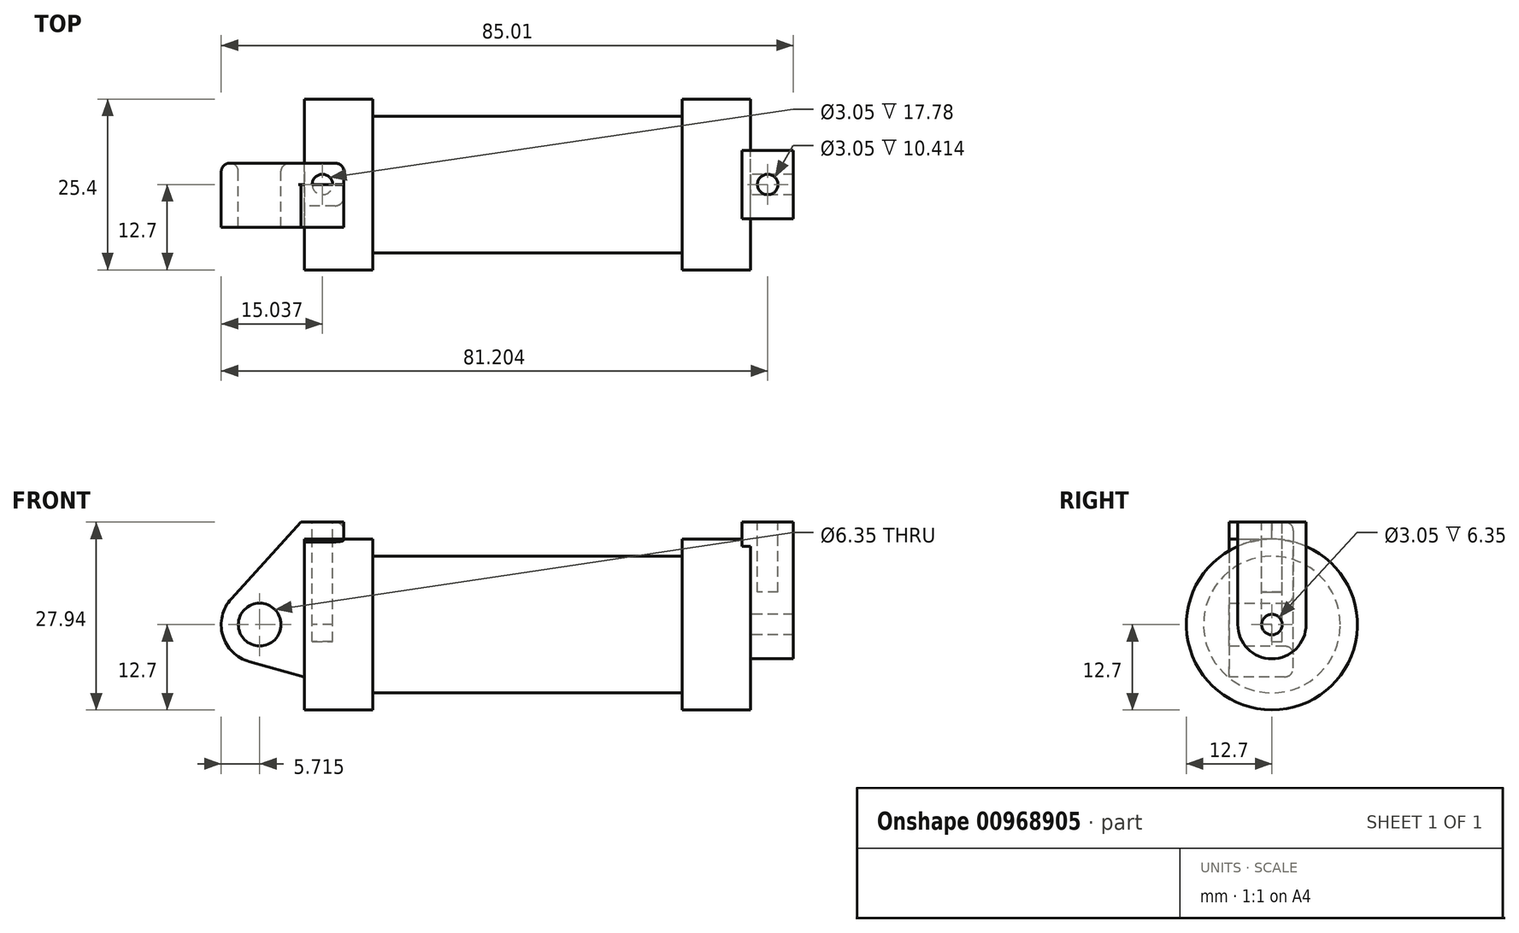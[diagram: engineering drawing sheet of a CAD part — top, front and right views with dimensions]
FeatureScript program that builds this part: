
annotation { "Feature Type Name" : "Feature", "Feature Type Description" : "" }
export const myFeature = defineFeature(function(context is Context, id is Id, definition is map)
    precondition{}
    {
        {
            var Q0;
            Q0=qCreatedBy(makeId("Front.planeOp"),FACE);
            var sketch = newSketch(context, id + "F0", { "sketchPlane" : qUnion([Q0])});
            skLineSegment(sketch, "E0", {"start": v(0, 0) * mm, "end": v(0, 12.7) * mm});
            skLineSegment(sketch, "E1", {"start": v(0, 12.7) * mm, "end": v(10.16, 12.7) * mm});
            skLineSegment(sketch, "E2", {"start": v(10.16, 12.7) * mm, "end": v(10.16, 10.16) * mm});
            skLineSegment(sketch, "E3", {"start": v(10.16, 10.16) * mm, "end": v(56.13, 10.16) * mm});
            skLineSegment(sketch, "E4", {"start": v(56.13, 10.16) * mm, "end": v(56.13, 12.7) * mm});
            skLineSegment(sketch, "E5", {"start": v(56.13, 12.7) * mm, "end": v(66.3, 12.7) * mm});
            skLineSegment(sketch, "E6", {"start": v(66.3, 12.7) * mm, "end": v(66.3, 0) * mm});
            skLineSegment(sketch, "E7", {"start": v(66.3, 0) * mm, "end": v(0, 0) * mm});
            skLineSegment(sketch, "E8", {"start": v(5.84, 15.24) * mm, "end": v(-0.5, 15.24) * mm});
            skLineSegment(sketch, "E9", {"start": v(-0.5, 15.24) * mm, "end": v(-10.88, 3.85) * mm});
            skLineSegment(sketch, "E10", {"start": v(0, 0) * mm, "end": v(-6.65, 0) * mm});
            skCircle(sketch, "E11", {"center": v(-6.65, 0) * mm, "radius": 5.72 * mm});
            skCircle(sketch, "E12", {"center": v(-6.65, 0) * mm, "radius": 3.18 * mm});
            skLineSegment(sketch, "E13", {"start": v(5.84, 15.24) * mm, "end": v(5.84, -9.4) * mm});
            skLineSegment(sketch, "E14", {"start": v(5.84, -9.4) * mm, "end": v(-8.18, -5.5) * mm});
            skSolve(sketch);
        }
        {
            var Q0;
            {var subQ1=sQuery(id+"F0.wireOp",EDGE,"E0");Q0=makeQuery(id+"F0.imprint","IMPRINT",FACE,{"disambiguationData":[TD([[makeQuery(id+"F0.imprint","IMPRINT",EDGE,{"derivedFrom":subQ1}),1.0]])]});}
            var Q1;
            {var subQ0=sQuery(id+"F0.wireOp",EDGE,"E0");Q1=makeQuery(id+"F0.imprint","IMPRINT",FACE,{"disambiguationData":[TD([[makeQuery(id+"F0.imprint","IMPRINT",EDGE,{"derivedFrom":subQ0}),-1.0]])]});}
            var Q2;
            {var subQ0=sQuery(id+"F0.wireOp",EDGE,"E14");Q2=makeQuery(id+"F0.imprint","IMPRINT",FACE,{"disambiguationData":[TD([[makeQuery(id+"F0.imprint","IMPRINT",EDGE,{"derivedFrom":subQ0}),-1.0]])]});}
            var Q3;
            {var subQ5=sQuery(id+"F0.wireOp",EDGE,"E12");Q3=makeQuery(id+"F0.imprint","IMPRINT",FACE,{"disambiguationData":[TD([[makeQuery(id+"F0.imprint","IMPRINT",EDGE,{"derivedFrom":subQ5}),-1.0]])]});}
            extrude(context, id + "F1", {"entities" : qUnion([Q0, Q1, Q2, Q3]), "endBound" : BoundingType.SYMMETRIC, "depth" : 6.35 * mm, "offsetDistance" : 25.4 * mm});
        }
        {
            var Q0;
            {var subQ0=sQuery(id+"F0.wireOp",EDGE,"E2");Q0=makeQuery(id+"F0.imprint","IMPRINT",FACE,{"disambiguationData":[TD([[makeQuery(id+"F0.imprint","IMPRINT",EDGE,{"derivedFrom":subQ0}),-1.0]])]});}
            var Q1;
            {var subQ0=sQuery(id+"F0.wireOp",EDGE,"E0");Q1=makeQuery(id+"F0.imprint","IMPRINT",FACE,{"disambiguationData":[TD([[makeQuery(id+"F0.imprint","IMPRINT",EDGE,{"derivedFrom":subQ0}),-1.0]])]});}
            var Q2;
            Q2=sQuery(id+"F0.wireOp",EDGE,"E7");
            revolve(context, id + "F2", {"surfaceOperationType" : NewSurfaceOperationType.NEW, "entities" : qUnion([Q0, Q1]), "axis" : qUnion([Q2]), "revolveType" : RevolveType.FULL});
        }
        {
            var Q0;
            Q0=makeQuery(id+"F2.opRevolve","SWEPT_FACE",FACE,{"disambiguationData":[OSD([sQuery(id+"F0.wireOp",EDGE,"E6")])]});
            var sketch = newSketch(context, id + "F3", { "sketchPlane" : qUnion([Q0])});
            skCircle(sketch, "E15", {"center": v(0, 0) * mm, "radius": 1.52 * mm});
            skCircle(sketch, "E16", {"center": v(0, 0) * mm, "radius": 5.08 * mm});
            skLineSegment(sketch, "E17", {"start": v(5.08, 0) * mm, "end": v(5.08, 15.24) * mm});
            skLineSegment(sketch, "E18", {"start": v(-5.08, 0) * mm, "end": v(-5.08, 15.24) * mm});
            skLineSegment(sketch, "E19", {"start": v(-5.08, 15.24) * mm, "end": v(5.08, 15.24) * mm});
            skSolve(sketch);
        }
        {
            var Q0;
            {var subQ0=sQuery(id+"F3.wireOp",EDGE,"E19");Q0=makeQuery(id+"F3.imprint","IMPRINT",FACE,{"disambiguationData":[TD([[makeQuery(id+"F3.imprint","IMPRINT",EDGE,{"derivedFrom":subQ0}),-1.0]])]});}
            extrude(context, id + "F4", {"entities" : qUnion([Q0]), "operationType" : NewBodyOperationType.ADD, "depth" : -1.27 * mm, "offsetDistance" : 25.4 * mm});
        }
        {
            var Q0;
            Q0 = qSketchRegion(id + "F3", true);
            extrude(context, id + "F5", {"entities" : qUnion([Q0]), "operationType" : NewBodyOperationType.ADD, "depth" : 6.35 * mm, "offsetDistance" : 25.4 * mm});
        }
        {
            var Q0;
            Q0=makeQuery(id+"F1.opExtrude","SWEPT_FACE",FACE,{"disambiguationData":[OSD([sQuery(id+"F0.wireOp",EDGE,"E8")])]});
            var sketch = newSketch(context, id + "F6", { "sketchPlane" : qUnion([Q0])});
            skLineSegment(sketch, "E20", {"start": v(2.67, 3.18) * mm, "end": v(2.67, -3.18) * mm, "construction": true});
            skCircle(sketch, "E21", {"center": v(2.67, 0) * mm, "radius": 1.52 * mm});
            skSolve(sketch);
        }
        {
            var Q0;
            Q0=makeQuery(id+"F6.imprint","IMPRINT",FACE,{"disambiguationData":[TD([[makeQuery(id+"F6.imprint","IMPRINT",EDGE,{"derivedFrom":sQuery(id+"F6.wireOp",EDGE,"E21")}),1.0]])]});
            extrude(context, id + "F7", {"entities" : qUnion([Q0]), "operationType" : NewBodyOperationType.REMOVE, "oppositeDirection" : true, "depth" : 17.78 * mm, "offsetDistance" : 25.4 * mm});
        }
        {
            var Q0;
            {var subQ0=sQuery(id+"F3.wireOp",EDGE,"E19");Q0=makeQuery(id+"F5.boolean.opBoolean","MERGE",FACE,{"derivedFrom":[makeQuery(id+"F4.opExtrude","SWEPT_FACE",FACE,{"disambiguationData":[OSD([subQ0])]}),makeQuery(id+"F5.opExtrude","SWEPT_FACE",FACE,{"disambiguationData":[OSD([subQ0])]})]});}
            var sketch = newSketch(context, id + "F8", { "sketchPlane" : qUnion([Q0])});
            skLineSegment(sketch, "E22", {"start": v(68.83, 5.08) * mm, "end": v(68.83, -5.08) * mm, "construction": true});
            skCircle(sketch, "E23", {"center": v(68.83, 0) * mm, "radius": 1.52 * mm});
            skSolve(sketch);
        }
        {
            var Q0;
            Q0 = qSketchRegion(id + "F8", true);
            extrude(context, id + "F9", {"entities" : qUnion([Q0]), "operationType" : NewBodyOperationType.REMOVE, "oppositeDirection" : true, "depth" : 10.4 * mm, "offsetDistance" : 25.4 * mm});
        }
        {
            var Q0;
            Q0=makeQuery(id+"F1.opExtrude","SWEPT_FACE",FACE,{"disambiguationData":[OSD([sQuery(id+"F0.wireOp",EDGE,"E9")])]});
            var Q1;
            Q1=makeQuery(id+"F1.opExtrude","CAP_EDGE",EDGE,{"disambiguationData":[OSD([sQuery(id+"F0.wireOp",EDGE,"E8")])],"isStart":true});
            var Q2;
            Q2=makeQuery(id+"F1.opExtrude","CAP_EDGE",EDGE,{"disambiguationData":[OSD([sQuery(id+"F0.wireOp",EDGE,"E13")])],"isStart":true});
            var Q3;
            Q3=makeQuery(id+"F1.opExtrude","SWEPT_EDGE",EDGE,{"disambiguationData":[OSD([sQuery(id+"F0.wireOp",EDGE,"E8"),sQuery(id+"F0.wireOp",EDGE,"E13")])]});
            var Q4;
            Q4=makeQuery(id+"F1.opExtrude","CAP_EDGE",EDGE,{"disambiguationData":[OSD([sQuery(id+"F0.wireOp",EDGE,"E13")])],"isStart":false});
            var Q5;
            Q5=makeQuery(id+"F1.opExtrude","CAP_EDGE",EDGE,{"disambiguationData":[OSD([sQuery(id+"F0.wireOp",EDGE,"E8")])],"isStart":false});
            var Q6;
            Q6=makeQuery(id+"F2.opRevolve","SWEPT_EDGE",EDGE,{"disambiguationData":[OSD([sQuery(id+"F0.wireOp",EDGE,"E1"),sQuery(id+"F0.wireOp",EDGE,"E2")])]});
            var Q7;
            Q7=makeQuery(id+"F2.opRevolve","SWEPT_EDGE",EDGE,{"disambiguationData":[OSD([sQuery(id+"F0.wireOp",EDGE,"E2"),sQuery(id+"F0.wireOp",EDGE,"E3")])]});
            var Q8;
            Q8=makeQuery(id+"F5.opExtrude","SWEPT_FACE",FACE,{"disambiguationData":[OSD([sQuery(id+"F3.wireOp",EDGE,"E16")])]});
            var Q9;
            {var subQ0=sQuery(id+"F3.wireOp",EDGE,"E19");var subQ1=sQuery(id+"F3.wireOp",EDGE,"E17");Q9=makeQuery(id+"F5.boolean.opBoolean","MERGE",EDGE,{"derivedFrom":[makeQuery(id+"F4.opExtrude","SWEPT_EDGE",EDGE,{"disambiguationData":[OSD([subQ1,subQ0])]}),makeQuery(id+"F5.opExtrude","SWEPT_EDGE",EDGE,{"disambiguationData":[OSD([subQ1,subQ0])]})]});}
            var Q10;
            Q10=makeQuery(id+"F4.opExtrude","CAP_EDGE",EDGE,{"disambiguationData":[OSD([sQuery(id+"F3.wireOp",EDGE,"E17")])],"isStart":false});
            var Q11;
            Q11=makeQuery(id+"F2.opRevolve","SWEPT_EDGE",EDGE,{"disambiguationData":[OSD([sQuery(id+"F0.wireOp",EDGE,"E4"),sQuery(id+"F0.wireOp",EDGE,"E5")])]});
            var Q12;
            Q12=makeQuery(id+"F2.opRevolve","SWEPT_EDGE",EDGE,{"disambiguationData":[OSD([sQuery(id+"F0.wireOp",EDGE,"E3"),sQuery(id+"F0.wireOp",EDGE,"E4")])]});
            var Q13;
            Q13=makeQuery(id+"F4.opExtrude","CAP_EDGE",EDGE,{"disambiguationData":[OSD([sQuery(id+"F3.wireOp",EDGE,"E19")])],"isStart":false});
            var Q14;
            Q14=makeQuery(id+"F4.opExtrude","CAP_EDGE",EDGE,{"disambiguationData":[OSD([sQuery(id+"F3.wireOp",EDGE,"E18")])],"isStart":false});
            var Q15;
            {var subQ0=sQuery(id+"F3.wireOp",EDGE,"E19");var subQ1=sQuery(id+"F3.wireOp",EDGE,"E18");Q15=makeQuery(id+"F5.boolean.opBoolean","MERGE",EDGE,{"derivedFrom":[makeQuery(id+"F4.opExtrude","SWEPT_EDGE",EDGE,{"disambiguationData":[OSD([subQ1,subQ0])]}),makeQuery(id+"F5.opExtrude","SWEPT_EDGE",EDGE,{"disambiguationData":[OSD([subQ1,subQ0])]})]});}
            var Q16;
            Q16=makeQuery(id+"F5.opExtrude","CAP_EDGE",EDGE,{"disambiguationData":[OSD([sQuery(id+"F3.wireOp",EDGE,"E19")])],"isStart":false});
            var Q17;
            Q17=makeQuery(id+"F2.opRevolve","SWEPT_EDGE",EDGE,{"disambiguationData":[OSD([sQuery(id+"F0.wireOp",EDGE,"E5"),sQuery(id+"F0.wireOp",EDGE,"E6")])]});
            var Q18;
            Q18=makeQuery(id+"F2.opRevolve","SWEPT_EDGE",EDGE,{"disambiguationData":[OSD([sQuery(id+"F0.wireOp",EDGE,"E0"),sQuery(id+"F0.wireOp",EDGE,"E1")])]});
            fillet(context, id + "F10", {"entities" : qUnion([Q0, Q1, Q2, Q3, Q4, Q5, Q6, Q7, Q8, Q9, Q10, Q11, Q12, Q13, Q14, Q15, Q16, Q17, Q18]), "radius" : 1.27 * mm, "tangentPropagation" : true, "allowEdgeOverflow" : false});
        }
        {
            var Q0;
            Q0=makeQuery(id+"F2.opRevolve","SWEPT_EDGE",EDGE,{"disambiguationData":[OSD([sQuery(id+"F0.wireOp",EDGE,"E1"),sQuery(id+"F0.wireOp",EDGE,"E2")])]});
            var Q1;
            Q1=makeQuery(id+"F2.opRevolve","SWEPT_EDGE",EDGE,{"disambiguationData":[OSD([sQuery(id+"F0.wireOp",EDGE,"E2"),sQuery(id+"F0.wireOp",EDGE,"E3")])]});
            var Q2;
            Q2=makeQuery(id+"F2.opRevolve","SWEPT_FACE",FACE,{"disambiguationData":[OSD([sQuery(id+"F0.wireOp",EDGE,"E3")])]});
            var Q3;
            Q3=makeQuery(id+"F2.opRevolve","SWEPT_FACE",FACE,{"disambiguationData":[OSD([sQuery(id+"F0.wireOp",EDGE,"E4")])]});
            var Q4;
            {var subQ0=sQuery(id+"F3.wireOp",EDGE,"E18");var subQ1=sQuery(id+"F3.wireOp",EDGE,"E17");var subQ2=sQuery(id+"F0.wireOp",EDGE,"E5");var subQ3=sQuery(id+"F0.wireOp",EDGE,"E6");Q4=makeQuery(id+"F5.boolean.opBoolean","SPLIT",FACE,{"disambiguationData":[TD([makeQuery(id+"F2.opRevolve","SWEPT_FACE",FACE,{"disambiguationData":[OSD([subQ2])]})])],"derivedFrom":makeQuery(id+"F4.boolean.opBoolean","MERGE",FACE,{"derivedFrom":[makeQuery(id+"F2.opRevolve","SWEPT_FACE",FACE,{"disambiguationData":[OSD([subQ3])]}),makeQuery(id+"F4.opExtrude","CAP_FACE",FACE,{"disambiguationData":[OSD([subQ2,subQ3,subQ1,subQ0,sQuery(id+"F3.wireOp",EDGE,"E19")])],"isStart":true})]})});}
            var Q5;
            Q5=makeQuery(id+"F1.opExtrude","SWEPT_EDGE",EDGE,{"disambiguationData":[OSD([sQuery(id+"F0.wireOp",EDGE,"E8"),sQuery(id+"F0.wireOp",EDGE,"E13")])]});
            var Q6;
            Q6=makeQuery(id+"F2.opRevolve","SWEPT_FACE",FACE,{"disambiguationData":[OSD([sQuery(id+"F0.wireOp",EDGE,"E1")])]});
            var Q7;
            Q7=makeQuery(id+"F2.opRevolve","SWEPT_EDGE",EDGE,{"disambiguationData":[OSD([sQuery(id+"F0.wireOp",EDGE,"E0"),sQuery(id+"F0.wireOp",EDGE,"E1")])]});
            var Q8;
            Q8=makeQuery(id+"F1.opExtrude","CAP_FACE",FACE,{"disambiguationData":[OSD([sQuery(id+"F0.wireOp",EDGE,"E8"),sQuery(id+"F0.wireOp",EDGE,"E9"),sQuery(id+"F0.wireOp",EDGE,"E11"),sQuery(id+"F0.wireOp",EDGE,"E12"),sQuery(id+"F0.wireOp",EDGE,"E13"),sQuery(id+"F0.wireOp",EDGE,"E14")])],"isStart":true});
            var Q9;
            {var subQ0=sQuery(id+"F3.wireOp",EDGE,"E19");Q9=makeQuery(id+"F5.boolean.opBoolean","MERGE",FACE,{"derivedFrom":[makeQuery(id+"F4.opExtrude","SWEPT_FACE",FACE,{"disambiguationData":[OSD([subQ0])]}),makeQuery(id+"F5.opExtrude","SWEPT_FACE",FACE,{"disambiguationData":[OSD([subQ0])]})]});}
            var Q10;
            Q10=makeQuery(id+"F5.opExtrude","CAP_EDGE",EDGE,{"disambiguationData":[OSD([sQuery(id+"F3.wireOp",EDGE,"E16")])],"isStart":false});
            var Q11;
            Q11=makeQuery(id+"F1.opExtrude","SWEPT_FACE",FACE,{"disambiguationData":[OSD([sQuery(id+"F0.wireOp",EDGE,"E9")])]});
            var Q12;
            Q12=makeQuery(id+"F1.opExtrude","CAP_EDGE",EDGE,{"disambiguationData":[OSD([sQuery(id+"F0.wireOp",EDGE,"E8")])],"isStart":false});
            var Q13;
            Q13=makeQuery(id+"F1.opExtrude","CAP_FACE",FACE,{"disambiguationData":[OSD([sQuery(id+"F0.wireOp",EDGE,"E8"),sQuery(id+"F0.wireOp",EDGE,"E9"),sQuery(id+"F0.wireOp",EDGE,"E11"),sQuery(id+"F0.wireOp",EDGE,"E12"),sQuery(id+"F0.wireOp",EDGE,"E13"),sQuery(id+"F0.wireOp",EDGE,"E14")])],"isStart":true});
            var Q14;
            Q14=makeQuery(id+"F1.opExtrude","SWEPT_FACE",FACE,{"disambiguationData":[OSD([sQuery(id+"F0.wireOp",EDGE,"E13")])]});
            var Q15;
            Q15=makeQuery(id+"F5.opExtrude","CAP_EDGE",EDGE,{"disambiguationData":[OSD([sQuery(id+"F3.wireOp",EDGE,"E15")])],"isStart":true});
            fillet(context, id + "F11", {"entities" : qUnion([Q0, Q1, Q2, Q3, Q4, Q5, Q6, Q7, Q8, Q9, Q10, Q11, Q12, Q13, Q14, Q15]), "radius" : 1.27 * mm, "tangentPropagation" : true, "allowEdgeOverflow" : false});
        }
        {
            var Q0;
            {var subQ5=sQuery(id+"F0.wireOp",EDGE,"E12");Q0=makeQuery(id+"F0.imprint","IMPRINT",FACE,{"disambiguationData":[TD([[makeQuery(id+"F0.imprint","IMPRINT",EDGE,{"derivedFrom":subQ5}),-1.0]])]});}
            var Q1;
            {var subQ0=sQuery(id+"F0.wireOp",EDGE,"E14");Q1=makeQuery(id+"F0.imprint","IMPRINT",FACE,{"disambiguationData":[TD([[makeQuery(id+"F0.imprint","IMPRINT",EDGE,{"derivedFrom":subQ0}),-1.0]])]});}
            extrude(context, id + "F12", {"entities" : qUnion([Q0, Q1]), "operationType" : NewBodyOperationType.ADD, "depth" : 6.35 * mm, "offsetDistance" : 25.4 * mm});
        }
        {
            var Q0;
            {var subQ1=sQuery(id+"F0.wireOp",EDGE,"E0");Q0=makeQuery(id+"F0.imprint","IMPRINT",FACE,{"disambiguationData":[TD([[makeQuery(id+"F0.imprint","IMPRINT",EDGE,{"derivedFrom":subQ1}),1.0]])]});}
            extrude(context, id + "F13", {"entities" : qUnion([Q0]), "operationType" : NewBodyOperationType.ADD, "depth" : 6.35 * mm, "offsetDistance" : 25.4 * mm});
        }
    });
